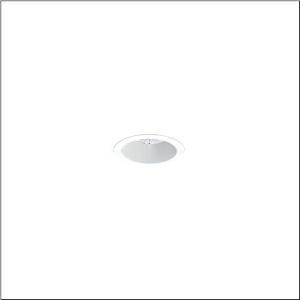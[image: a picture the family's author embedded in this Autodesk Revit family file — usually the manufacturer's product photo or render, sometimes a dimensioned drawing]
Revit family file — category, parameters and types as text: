
# Revit family: lunis_21_s_51db18ea91c
name_source: partatom
category: Lighting Fixtures
units: mm (PartAtom-declared; Revit-internal decimal feet)

## family parameters
Cut with Voids When Loaded = No
Host = Face
Light Source = No
Part Type = Normal
Room Calculation Point = No
Round Connector Dimension = Use Diameter
Shared = No

## types (1)
- --- (1 x LED, 1060 lm, 8 W, 6500K)
    Apparent Load = 8 VA
    CIE Flux Codes = 86 95 99 100 100
    Color Rendering = 80
    Color Temperature = 6500K
    Default Elevation = 1800 mm
    Description = Lunis 21,  S, downlight, light control with lens, of PMMA, anti glare with reflector, of PC, light emission: direct distribution, LED rated luminous flux: 950lm, light colour: 830/840/865, with terminal, 5-pole, mains connection: 220..240V, AC, 50..60Hz, housing, round, of diecast aluminium, traffic white (RAL 9016), diameter: 84mm, clamping range: 1..40mm, protection rating (complete): IP20, protection rating (on room side): IP54, insulation class (complete): insulation class II (safety insulation), certification: CE, impact resistance: IK03, packaging unit: 1 piece
    Height = 0 mm  [stored 0 ft]
    Lamp = 1 x LED
    Lamp Light Flux = 1060 lm
    Lamp Power = 8 W
    Lamp count = 1
    Length = 84 mm
    Luminous efficacy = 133 lm/W
    Manufacturer = Siteco
    ModVariant = No
    Model = 51DB18EA91C
    Mounting Place = Ceiling
    Mounting Type = Recessed
    Number of Poles = 1
    OnlyDefault = Yes
    Power Factor = 1
    Product Name = Lunis 21 S
    Product group = downlight
    ProductGroupID = 400
    Protection Class = Protection class II
    Protection Degree = IP 20
    RLX_Detail_Level = 1
    RLX_Emergency_Light_Flux = 0 lm
    RLX_Emergency_Type = 0
    RLX_Emergency_Type_DB = No
    RlxData = <blob elided: 8937 chars, md5=972704e9>
    Socket = socket
    Standby Power = 0 W
    System Light Flux = 1060 lm
    System Power = 8 W
    Type Comments = individual setting: colour temperature 6500K, luminous flux: 100 % | (OFF | OFF | ON | OFF) | 200 mA
    Type Image = l_1290842.jpg
    URL = http://relux.com
    VarID = @adj_019700
    Voltage = 0 V
    Weight = 0.00 kg
    Width = 0 mm  [stored 0 ft]

note: [stored X ft] marks values corroborated as IEEE doubles in the binary element streams (Revit-internal decimal feet)

## geometry (parser evidence)
native form markers: Sweep x9
no freeform markers — native parametric forms only
